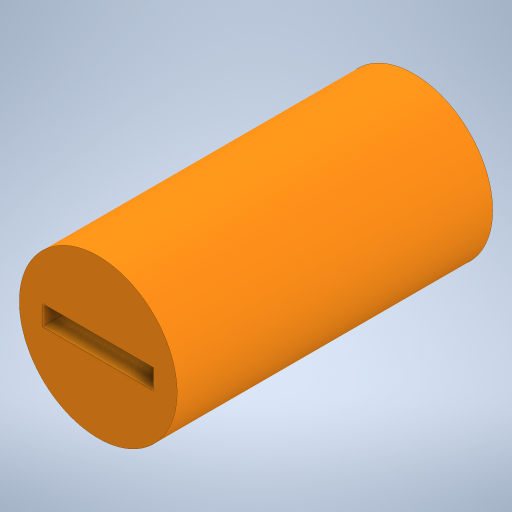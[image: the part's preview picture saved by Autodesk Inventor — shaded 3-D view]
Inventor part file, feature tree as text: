
AUTODESK INVENTOR PART (.ipt)
format: ipt  version: 2023 (Build 270158000, 158)  size: 232,960 bytes
history: native  units: in
note: dims shown in document units (in); Inventor stores cm internally (conversion verified against a paired STEP export)
features: extrude x3, sketch x3, other x3, reference x1
ambient origin geometry x8: Origin, YZ Plane, XZ Plane, XY Plane, X Axis, Y Axis, Z Axis, Center Point
bodies: Solid1 (feature_tree)
feature tree (10):
  extrude  "Extrusion1"  Depth=0.2441in
  extrude  "Extrusion2"  Depth=0.3937in TaperAngle=0.0deg
  extrude  "Extrusion3"  Depth=0.0984in
  sketch  "Sketch1"  dims[d0=0.7874in d1=0.2441in]
  reference  "Reference1"
  sketch  "Sketch2"  dims[d2=0.0079in d3=0.3937in d4=0.0in]
  sketch  "Sketch3"  dims[d5=0.5906in d6=0.0in d7=0.0984in d8=0.5512in d9=0.0492in d10=0.2756in d11=0.5906in d12=0.0in]
  other  "<userpath>\OneDrive\Objet3D\3DPrinter\3DPrinterBeltCoreXY.iam"
  other  "3DPrinterBeltCoreXY.iam"
  other  "DCMotor:1"
